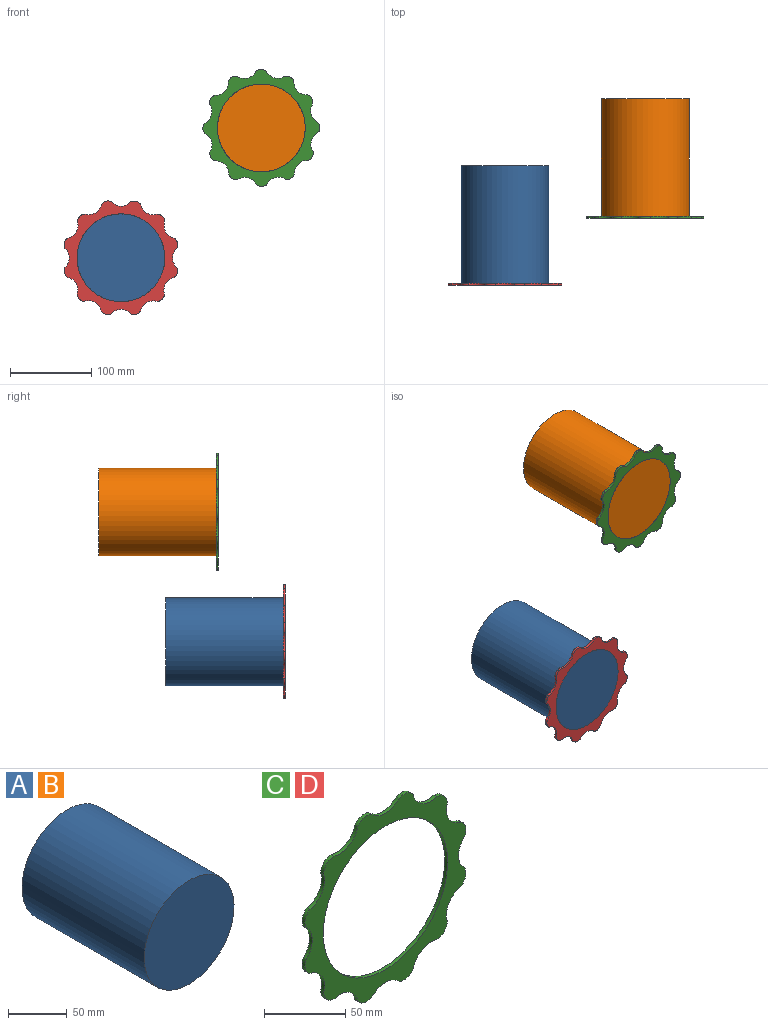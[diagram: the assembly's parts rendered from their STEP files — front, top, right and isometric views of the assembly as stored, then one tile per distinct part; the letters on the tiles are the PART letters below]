
ASSEMBLY  parts=4 mates=1
PART A: 3 faces, bbox 108x147x108 mm
  f0: cylinder r=53.98mm len=147mm, axis (0,1,0), area 49853.4mm2, adj f1,f2
  f1: plane 107.95x107.95mm, normal (0,-1,0), area 9152.4mm2, adj f0
  f2: plane 107.95x107.95mm, normal (0,1,0), area 9152.4mm2, adj f0
PART B: same geometry as A
PART C: 27 faces, bbox 139.7x2.5x139.7 mm
  f0: cylinder r=9.59mm len=8.98mm, axis (0,1,0), area 35.3mm2, adj f1,f23,f25,f26
  f1: cylinder r=15.88mm len=20.56mm, axis (0,1,0), area 68.1mm2, adj f0,f2,f25,f26
  f2: cylinder r=9.59mm len=12.27mm, axis (0,1,0), area 35.3mm2, adj f1,f3,f25,f26
  f3: cylinder r=15.88mm len=23.74mm, axis (0,1,0), area 68.1mm2, adj f2,f4,f25,f26
  f4: cylinder r=9.59mm len=12.27mm, axis (0,1,0), area 35.3mm2, adj f3,f5,f25,f26
  f5: cylinder r=15.88mm len=20.56mm, axis (0,1,0), area 68.1mm2, adj f4,f6,f25,f26
  f6: cylinder r=9.59mm len=8.98mm, axis (0,1,0), area 35.3mm2, adj f5,f7,f25,f26
  f7: cylinder r=15.88mm len=20.56mm, axis (0,1,0), area 68.1mm2, adj f6,f8,f25,f26
  f8: cylinder r=9.59mm len=12.27mm, axis (0,1,0), area 35.3mm2, adj f7,f9,f25,f26
  f9: cylinder r=15.88mm len=23.74mm, axis (0,1,0), area 68.1mm2, adj f8,f10,f25,f26
  f10: cylinder r=9.59mm len=12.27mm, axis (0,1,0), area 35.3mm2, adj f9,f11,f25,f26
  f11: cylinder r=15.88mm len=20.56mm, axis (0,1,0), area 68.1mm2, adj f10,f12,f25,f26
  f12: cylinder r=9.59mm len=8.98mm, axis (0,1,0), area 35.3mm2, adj f11,f13,f25,f26
  f13: cylinder r=15.88mm len=20.56mm, axis (0,1,0), area 68.1mm2, adj f12,f14,f25,f26
  f14: cylinder r=9.59mm len=12.27mm, axis (0,1,0), area 35.3mm2, adj f13,f15,f25,f26
  f15: cylinder r=15.88mm len=23.74mm, axis (0,1,0), area 68.1mm2, adj f14,f16,f25,f26
  f16: cylinder r=9.59mm len=12.27mm, axis (0,1,0), area 35.3mm2, adj f15,f17,f25,f26
  f17: cylinder r=15.88mm len=20.56mm, axis (0,1,0), area 68.1mm2, adj f16,f18,f25,f26
  f18: cylinder r=9.59mm len=8.98mm, axis (0,1,0), area 35.3mm2, adj f17,f19,f25,f26
  f19: cylinder r=15.88mm len=20.56mm, axis (0,1,0), area 68.1mm2, adj f18,f20,f25,f26
  f20: cylinder r=9.59mm len=12.27mm, axis (0,1,0), area 35.3mm2, adj f19,f21,f25,f26
  f21: cylinder r=15.88mm len=23.74mm, axis (0,1,0), area 68.1mm2, adj f20,f22,f25,f26
  f22: cylinder r=9.59mm len=12.27mm, axis (0,1,0), area 35.3mm2, adj f21,f23,f25,f26
  f23: cylinder r=15.88mm len=20.56mm, axis (0,1,0), area 68.1mm2, adj f0,f22,f25,f26
  f24: cylinder r=53.98mm len=107.95mm, axis (0,1,0), area 861.4mm2, adj f25,f26
  f25: plane 139.68x139.68mm, normal (0,-1,0), area 5151.2mm2, adj f0,f1,f2,f3,f4,f5,f6,f7
  f26: plane 139.68x139.68mm, normal (0,1,0), area 5151.2mm2, adj f0,f1,f2,f3,f4,f5,f6,f7
PART D: same geometry as C
PLACE A t=(-25,-25.23,-17.07)mm
PLACE B t=(147.61,56.84,142.62)mm
PLACE C rot(axis=(0,-1,0),45.4deg) t=(147.61,-87.63,142.62)mm
PLACE D rot(axis=(0,1,0),30.1deg) t=(-25,-169.69,-17.07)mm
MATE revolute C.f24 <-> B.f0  axis (0,-1,0) through (147.61,-90.17,142.62)mm
